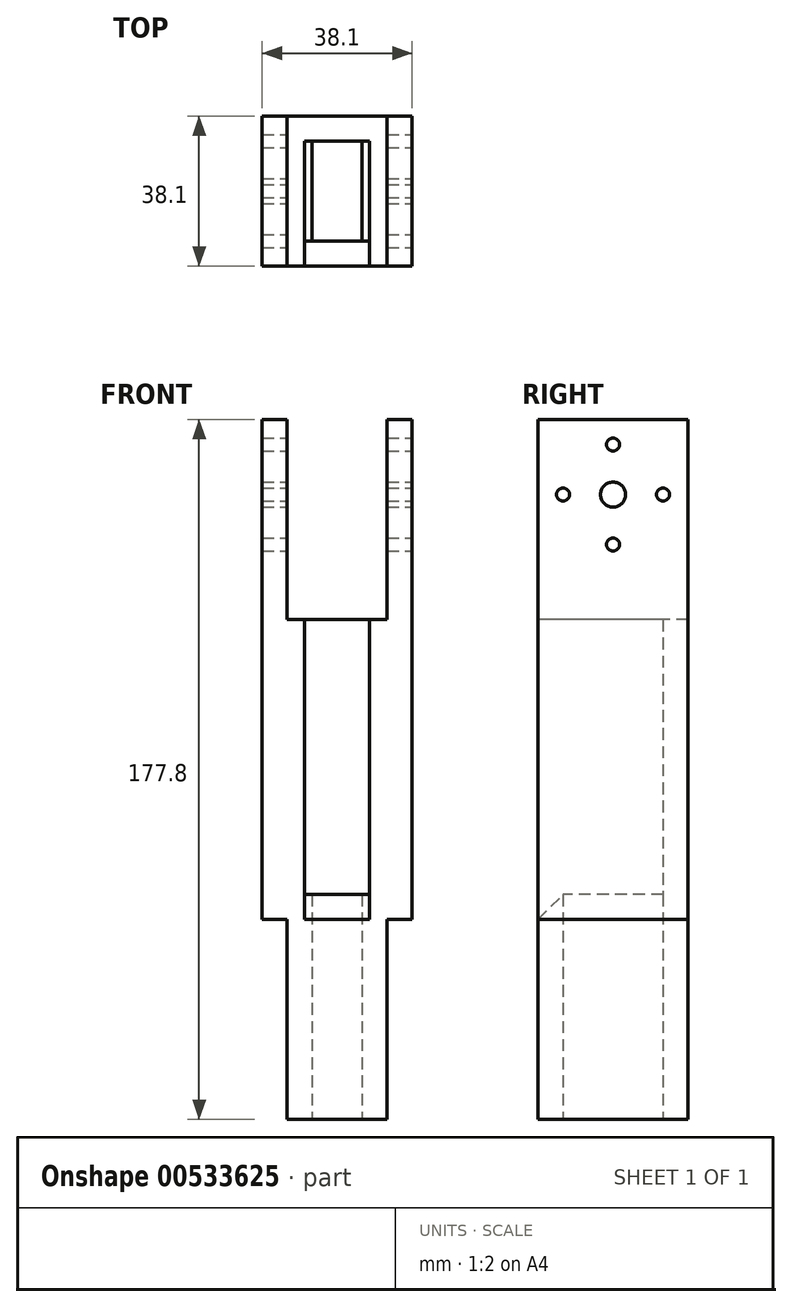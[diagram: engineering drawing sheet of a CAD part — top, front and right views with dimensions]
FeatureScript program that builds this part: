
annotation { "Feature Type Name" : "Feature", "Feature Type Description" : "" }
export const myFeature = defineFeature(function(context is Context, id is Id, definition is map)
    precondition{}
    {
        {
            var Q0;
            Q0=qCreatedBy(makeId("Top.planeOp"),FACE);
            var sketch = newSketch(context, id + "F0", { "sketchPlane" : qUnion([Q0])});
            skLineSegment(sketch, "E0.bottom", {"start": v(-6.35, 12.7) * mm, "end": v(6.35, 12.7) * mm});
            skLineSegment(sketch, "E0.top", {"start": v(-6.35, -12.7) * mm, "end": v(6.35, -12.7) * mm});
            skLineSegment(sketch, "E0.left", {"start": v(-6.35, 12.7) * mm, "end": v(-6.35, -12.7) * mm});
            skLineSegment(sketch, "E0.right", {"start": v(6.35, 12.7) * mm, "end": v(6.35, -12.7) * mm});
            skPoint(sketch, "E0.middle", {"position": v(0, 0) * mm});
            skLineSegment(sketch, "E1.0", {"start": v(-12.7, 19.05) * mm, "end": v(12.7, 19.05) * mm});
            skLineSegment(sketch, "E1.1", {"start": v(-12.7, 19.05) * mm, "end": v(-12.7, -19.05) * mm});
            skLineSegment(sketch, "E1.2", {"start": v(-12.7, -19.05) * mm, "end": v(12.7, -19.05) * mm});
            skLineSegment(sketch, "E1.3", {"start": v(12.7, 19.05) * mm, "end": v(12.7, -19.05) * mm});
            skLineSegment(sketch, "E2", {"start": v(-12.7, 19.05) * mm, "end": v(-19.05, 19.05) * mm});
            skLineSegment(sketch, "E3", {"start": v(-19.05, 19.05) * mm, "end": v(-19.05, -19.05) * mm});
            skLineSegment(sketch, "E4", {"start": v(-19.05, -19.05) * mm, "end": v(-12.7, -19.05) * mm});
            skLineSegment(sketch, "E5.MirrorCS", {"start": v(12.7, 19.05) * mm, "end": v(19.05, 19.05) * mm});
            skLineSegment(sketch, "E6.MirrorCS", {"start": v(19.05, 19.05) * mm, "end": v(19.05, -19.05) * mm});
            skLineSegment(sketch, "E7.MirrorCS", {"start": v(19.05, -19.05) * mm, "end": v(12.7, -19.05) * mm});
            skLineSegment(sketch, "E8", {"start": v(-8.25, 19.05) * mm, "end": v(-8.26, -19.05) * mm});
            skLineSegment(sketch, "E9.MirrorCS", {"start": v(8.26, 19.05) * mm, "end": v(8.26, -19.05) * mm});
            skLineSegment(sketch, "E10", {"start": v(-8.26, 12.7) * mm, "end": v(-6.35, 12.7) * mm});
            skLineSegment(sketch, "E11", {"start": v(6.35, 12.7) * mm, "end": v(8.26, 12.7) * mm});
            skSolve(sketch);
        }
        {
            var Q0;
            Q0=makeQuery(id+"F0.imprint","IMPRINT",FACE,{"disambiguationData":[TD([[makeQuery(id+"F0.imprint","IMPRINT",EDGE,{"derivedFrom":sQuery(id+"F0.wireOp",EDGE,"E0.top")}),-1.0]])]});
            extrude(context, id + "F1", {"entities" : qUnion([Q0]), "depth" : 6.35 * mm, "offsetDistance" : 25.4 * mm});
        }
        {
            var Q0;
            {var subQ0=sQuery(id+"F0.wireOp",EDGE,"E1.1");Q0=makeQuery(id+"F0.imprint","IMPRINT",FACE,{"disambiguationData":[TD([[makeQuery(id+"F0.imprint","IMPRINT",EDGE,{"derivedFrom":subQ0}),1.0]])]});}
            var Q1;
            {var subQ0=sQuery(id+"F0.wireOp",EDGE,"E1.3");Q1=makeQuery(id+"F0.imprint","IMPRINT",FACE,{"disambiguationData":[TD([[makeQuery(id+"F0.imprint","IMPRINT",EDGE,{"derivedFrom":subQ0}),-1.0]])]});}
            var Q2;
            Q2=makeQuery(id+"F0.imprint","IMPRINT",FACE,{"disambiguationData":[TD([[makeQuery(id+"F0.imprint","IMPRINT",EDGE,{"derivedFrom":sQuery(id+"F0.wireOp",EDGE,"E0.bottom")}),1.0]])]});
            extrude(context, id + "F2", {"entities" : qUnion([Q0, Q1, Q2]), "operationType" : NewBodyOperationType.ADD, "depth" : 76.2 * mm, "offsetDistance" : 25.4 * mm});
        }
        {
            var Q0;
            Q0=makeQuery(id+"F0.imprint","IMPRINT",FACE,{"disambiguationData":[TD([[makeQuery(id+"F0.imprint","IMPRINT",EDGE,{"derivedFrom":sQuery(id+"F0.wireOp",EDGE,"E1.1")}),-1.0]])]});
            var Q1;
            Q1=makeQuery(id+"F0.imprint","IMPRINT",FACE,{"disambiguationData":[TD([[makeQuery(id+"F0.imprint","IMPRINT",EDGE,{"derivedFrom":sQuery(id+"F0.wireOp",EDGE,"E1.3")}),1.0]])]});
            extrude(context, id + "F3", {"entities" : qUnion([Q0, Q1]), "operationType" : NewBodyOperationType.ADD, "depth" : 127 * mm, "offsetDistance" : 25.4 * mm});
        }
        {
            var Q0;
            Q0=makeQuery(id+"F3.opExtrude","SWEPT_FACE",FACE,{"disambiguationData":[OSD([sQuery(id+"F0.wireOp",EDGE,"E6.MirrorCS")])]});
            var sketch = newSketch(context, id + "F4", { "sketchPlane" : qUnion([Q0])});
            skPoint(sketch, "E12", {"position": v(0, 107.95) * mm});
            skCircle(sketch, "E13", {"center": v(0, 107.95) * mm, "radius": 12.7 * mm, "construction": true});
            skPoint(sketch, "E14", {"position": v(0, 120.65) * mm});
            skPoint(sketch, "E15", {"position": v(0, 95.25) * mm});
            skPoint(sketch, "E16", {"position": v(-12.7, 107.95) * mm});
            skPoint(sketch, "E17", {"position": v(12.7, 107.95) * mm});
            skSolve(sketch);
        }
        {
            var Q0;
            Q0=sQuery(id+"F4.wireOp",VERTEX,"E12");
            var Q1;
            Q1=makeQuery(id+"F1.opExtrude","SWEPT_BODY",BODY,{"disambiguationData":[OSD([sQuery(id+"F0.wireOp",EDGE,"E0.bottom"),sQuery(id+"F0.wireOp",EDGE,"E0.top"),sQuery(id+"F0.wireOp",EDGE,"E0.left"),sQuery(id+"F0.wireOp",EDGE,"E0.right"),sQuery(id+"F0.wireOp",EDGE,"E1.0"),sQuery(id+"F0.wireOp",EDGE,"E1.2"),sQuery(id+"F0.wireOp",EDGE,"E8"),sQuery(id+"F0.wireOp",EDGE,"E9.MirrorCS")])]});
            hole(context, id + "F5", {"style" : HoleStyle.SIMPLE, "endStyle" : HoleEndStyle.THROUGH, "holeDiameter" : 6.35 * mm, "isTappedThrough" : true, "tappedDepth" : 12.7 * mm, "tapClearance" : 3, "startFromSketch" : true, "locations" : qUnion([Q0]), "scope" : qUnion([Q1])});
        }
        {
            var Q0;
            Q0=makeQuery(id+"F1.opExtrude","CAP_EDGE",EDGE,{"disambiguationData":[OSD([sQuery(id+"F0.wireOp",EDGE,"E1.2")])],"isStart":false});
            var Q1;
            Q1=makeQuery(id+"F1.opExtrude","CAP_EDGE",EDGE,{"disambiguationData":[OSD([sQuery(id+"F0.wireOp",EDGE,"E1.0")])],"isStart":false});
            chamfer(context, id + "F6", {"entities" : qUnion([Q0, Q1]), "width" : 6.35 * mm, "tangentPropagation" : true});
        }
        {
            var Q0;
            Q0=sQuery(id+"F4.wireOp",VERTEX,"E14");
            var Q1;
            Q1=sQuery(id+"F4.wireOp",VERTEX,"E15");
            var Q2;
            Q2=sQuery(id+"F4.wireOp",VERTEX,"E17");
            var Q3;
            Q3=sQuery(id+"F4.wireOp",VERTEX,"E16");
            var Q4;
            Q4=makeQuery(id+"F1.opExtrude","SWEPT_BODY",BODY,{"disambiguationData":[OSD([sQuery(id+"F0.wireOp",EDGE,"E0.bottom"),sQuery(id+"F0.wireOp",EDGE,"E0.top"),sQuery(id+"F0.wireOp",EDGE,"E0.left"),sQuery(id+"F0.wireOp",EDGE,"E0.right"),sQuery(id+"F0.wireOp",EDGE,"E1.0"),sQuery(id+"F0.wireOp",EDGE,"E1.2"),sQuery(id+"F0.wireOp",EDGE,"E8"),sQuery(id+"F0.wireOp",EDGE,"E9.MirrorCS")])]});
            hole(context, id + "F7", {"style" : HoleStyle.SIMPLE, "endStyle" : HoleEndStyle.THROUGH, "holeDiameter" : 3.3 * mm, "isTappedThrough" : true, "tappedDepth" : 12.7 * mm, "tapClearance" : 3, "startFromSketch" : true, "locations" : qUnion([Q0, Q1, Q2, Q3]), "scope" : qUnion([Q4])});
        }
        {
            var Q0;
            Q0=makeQuery(id+"F0.imprint","IMPRINT",FACE,{"disambiguationData":[TD([[makeQuery(id+"F0.imprint","IMPRINT",EDGE,{"derivedFrom":sQuery(id+"F0.wireOp",EDGE,"E0.bottom")}),1.0]])]});
            var Q1;
            {var subQ4=sQuery(id+"F0.wireOp",EDGE,"E1.1");Q1=makeQuery(id+"F0.imprint","IMPRINT",FACE,{"disambiguationData":[TD([[makeQuery(id+"F0.imprint","IMPRINT",EDGE,{"derivedFrom":subQ4}),1.0]])]});}
            var Q2;
            Q2=makeQuery(id+"F0.imprint","IMPRINT",FACE,{"disambiguationData":[TD([[makeQuery(id+"F0.imprint","IMPRINT",EDGE,{"derivedFrom":sQuery(id+"F0.wireOp",EDGE,"E0.top")}),-1.0]])]});
            var Q3;
            {var subQ4=sQuery(id+"F0.wireOp",EDGE,"E1.3");Q3=makeQuery(id+"F0.imprint","IMPRINT",FACE,{"disambiguationData":[TD([[makeQuery(id+"F0.imprint","IMPRINT",EDGE,{"derivedFrom":subQ4}),-1.0]])]});}
            extrude(context, id + "F8", {"entities" : qUnion([Q0, Q1, Q2, Q3]), "operationType" : NewBodyOperationType.ADD, "oppositeDirection" : true, "depth" : 50.8 * mm, "offsetDistance" : 25.4 * mm});
        }
    });
